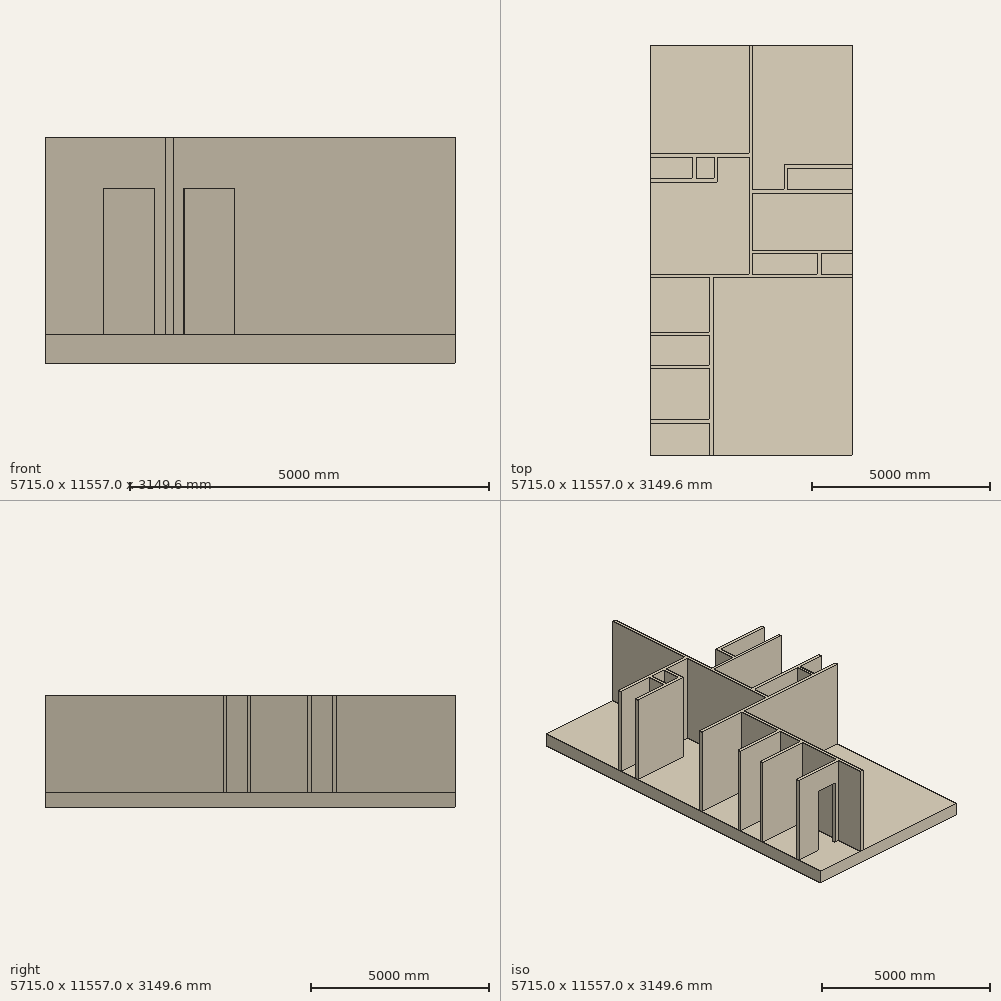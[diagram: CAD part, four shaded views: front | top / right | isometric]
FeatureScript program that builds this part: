
annotation { "Feature Type Name" : "Feature", "Feature Type Description" : "" }
export const myFeature = defineFeature(function(context is Context, id is Id, definition is map)
    precondition{}
    {
        {
            var Q0;
            Q0=qCreatedBy(makeId("Top.planeOp"),FACE);
            var sketch = newSketch(context, id + "F0", { "sketchPlane" : qUnion([Q0])});
            skLineSegment(sketch, "E0.bottom", {"start": v(-2857.5, 5778.5) * mm, "end": v(2857.5, 5778.5) * mm});
            skLineSegment(sketch, "E0.top", {"start": v(-2857.5, -5778.5) * mm, "end": v(2857.5, -5778.5) * mm});
            skLineSegment(sketch, "E0.left", {"start": v(-2857.5, 5778.5) * mm, "end": v(-2857.5, -5778.5) * mm});
            skLineSegment(sketch, "E0.right", {"start": v(2857.5, 5778.5) * mm, "end": v(2857.5, -5778.5) * mm});
            skLineSegment(sketch, "E1", {"start": v(-1079.5, -5778.5) * mm, "end": v(-1079.5, -774.7) * mm});
            skLineSegment(sketch, "E2", {"start": v(-1079.5, -774.7) * mm, "end": v(2857.5, -774.7) * mm});
            skLineSegment(sketch, "E3", {"start": v(-1181.1, -5778.5) * mm, "end": v(-1181.1, -4864.1) * mm});
            skLineSegment(sketch, "E4", {"start": v(-1181.1, -4864.1) * mm, "end": v(-2857.5, -4864.1) * mm});
            skLineSegment(sketch, "E5", {"start": v(-2857.5, -4762.5) * mm, "end": v(-1181.1, -4762.5) * mm});
            skLineSegment(sketch, "E6", {"start": v(-1181.1, -4762.5) * mm, "end": v(-1181.1, -3340.1) * mm});
            skLineSegment(sketch, "E7", {"start": v(-1181.1, -3340.1) * mm, "end": v(-2857.5, -3340.1) * mm});
            skLineSegment(sketch, "E8", {"start": v(-2857.5, -3238.5) * mm, "end": v(-1181.1, -3238.5) * mm});
            skLineSegment(sketch, "E9", {"start": v(-1181.1, -3238.5) * mm, "end": v(-1181.1, -2400.3) * mm});
            skLineSegment(sketch, "E10", {"start": v(-1181.1, -2400.3) * mm, "end": v(-2857.5, -2400.3) * mm});
            skLineSegment(sketch, "E11", {"start": v(-2857.5, -2298.7) * mm, "end": v(-1181.1, -2298.7) * mm});
            skLineSegment(sketch, "E12", {"start": v(-1181.1, -2298.7) * mm, "end": v(-1181.1, -774.7) * mm});
            skLineSegment(sketch, "E13", {"start": v(-1181.1, -774.7) * mm, "end": v(-2857.5, -774.7) * mm});
            skLineSegment(sketch, "E14", {"start": v(2857.5, -673.1) * mm, "end": v(1968.5, -673.1) * mm});
            skLineSegment(sketch, "E15", {"start": v(1968.5, -673.1) * mm, "end": v(1968.5, -88.9) * mm});
            skLineSegment(sketch, "E16", {"start": v(1968.5, -88.9) * mm, "end": v(2857.5, -88.9) * mm});
            skLineSegment(sketch, "E17", {"start": v(2857.5, 12.7) * mm, "end": v(38.1, 12.7) * mm});
            skLineSegment(sketch, "E18", {"start": v(38.1, 12.7) * mm, "end": v(38.1, 1612.9) * mm});
            skLineSegment(sketch, "E19", {"start": v(38.1, 1612.9) * mm, "end": v(2857.5, 1612.9) * mm});
            skLineSegment(sketch, "E20", {"start": v(1866.9, -673.1) * mm, "end": v(1866.9, -88.9) * mm});
            skLineSegment(sketch, "E21", {"start": v(1866.9, -88.9) * mm, "end": v(38.1, -88.9) * mm});
            skLineSegment(sketch, "E22", {"start": v(38.1, -88.9) * mm, "end": v(38.1, -673.1) * mm});
            skLineSegment(sketch, "E23", {"start": v(38.1, -673.1) * mm, "end": v(1866.9, -673.1) * mm});
            skLineSegment(sketch, "E24", {"start": v(-2857.5, -673.1) * mm, "end": v(-63.5, -673.1) * mm});
            skLineSegment(sketch, "E25", {"start": v(-63.5, -673.1) * mm, "end": v(-63.5, 2628.9) * mm});
            skLineSegment(sketch, "E26", {"start": v(-63.5, 2628.9) * mm, "end": v(-952.5, 2628.9) * mm});
            skLineSegment(sketch, "E27", {"start": v(-952.5, 2628.9) * mm, "end": v(-952.5, 1917.7) * mm});
            skLineSegment(sketch, "E28", {"start": v(-952.5, 1917.7) * mm, "end": v(-2857.5, 1917.7) * mm});
            skLineSegment(sketch, "E29.bottom", {"start": v(-1054.1, 2019.3) * mm, "end": v(-1562.1, 2019.3) * mm});
            skLineSegment(sketch, "E29.top", {"start": v(-1054.1, 2628.9) * mm, "end": v(-1562.1, 2628.9) * mm});
            skLineSegment(sketch, "E29.left", {"start": v(-1054.1, 2019.3) * mm, "end": v(-1054.1, 2628.9) * mm});
            skLineSegment(sketch, "E29.right", {"start": v(-1562.1, 2019.3) * mm, "end": v(-1562.1, 2628.9) * mm});
            skLineSegment(sketch, "E30", {"start": v(-2857.5, 2019.3) * mm, "end": v(-1663.7, 2019.3) * mm});
            skLineSegment(sketch, "E31", {"start": v(-1663.7, 2019.3) * mm, "end": v(-1663.7, 2628.9) * mm});
            skLineSegment(sketch, "E32", {"start": v(-1663.7, 2628.9) * mm, "end": v(-2857.5, 2628.9) * mm});
            skLineSegment(sketch, "E33", {"start": v(-2857.5, 2730.5) * mm, "end": v(-63.5, 2730.5) * mm});
            skLineSegment(sketch, "E34", {"start": v(-63.5, 2730.5) * mm, "end": v(-63.5, 5778.5) * mm});
            skLineSegment(sketch, "E35", {"start": v(38.1, 1714.5) * mm, "end": v(38.1, 5778.5) * mm});
            skLineSegment(sketch, "E36", {"start": v(38.1, 1714.5) * mm, "end": v(927.1, 1714.5) * mm});
            skLineSegment(sketch, "E37", {"start": v(927.1, 1714.5) * mm, "end": v(927.1, 2425.7) * mm});
            skLineSegment(sketch, "E38", {"start": v(927.1, 2425.7) * mm, "end": v(2857.5, 2425.7) * mm});
            skLineSegment(sketch, "E39", {"start": v(2857.5, 1714.5) * mm, "end": v(1028.7, 1714.5) * mm});
            skLineSegment(sketch, "E40", {"start": v(1028.7, 1714.5) * mm, "end": v(1028.7, 2324.1) * mm});
            skLineSegment(sketch, "E41", {"start": v(1028.7, 2324.1) * mm, "end": v(2857.5, 2324.1) * mm});
            skSolve(sketch);
        }
        {
            var Q0;
            Q0 = qSketchRegion(id + "F0", true);
            var Q1;
            Q1=makeQuery(id+"F0.imprint","IMPRINT",FACE,{"disambiguationData":[TD([[makeQuery(id+"F0.imprint","IMPRINT",EDGE,{"derivedFrom":sQuery(id+"F0.wireOp",EDGE,"E29.bottom")}),-1.0]])]});
            var Q2;
            Q2=makeQuery(id+"F0.imprint","IMPRINT",FACE,{"disambiguationData":[TD([[makeQuery(id+"F0.imprint","IMPRINT",EDGE,{"derivedFrom":sQuery(id+"F0.wireOp",EDGE,"E20")}),1.0]])]});
            extrude(context, id + "F1", {"entities" : qUnion([Q0, Q1, Q2]), "oppositeDirection" : true, "depth" : 406.4 * mm});
        }
        {
            var Q0;
            {var subQ19=sQuery(id+"F0.wireOp",EDGE,"E1");Q0=makeQuery(id+"F0.imprint","IMPRINT",FACE,{"disambiguationData":[TD([[makeQuery(id+"F0.imprint","IMPRINT",EDGE,{"derivedFrom":subQ19}),1.0]])]});}
            extrude(context, id + "F2", {"entities" : qUnion([Q0]), "depth" : 2743.2 * mm});
        }
        {
            var Q0;
            Q0=makeQuery(id+"F2.opExtrude","SWEPT_FACE",FACE,{"disambiguationData":[OSD([sQuery(id+"F0.wireOp",EDGE,"E2")])]});
            var sketch = newSketch(context, id + "F3", { "sketchPlane" : qUnion([Q0])});
            skLineSegment(sketch, "E42", {"start": v(-927.1, 0) * mm, "end": v(-927.1, 2032) * mm});
            skLineSegment(sketch, "E43", {"start": v(-927.1, 2032) * mm, "end": v(-215.9, 2032) * mm});
            skLineSegment(sketch, "E44", {"start": v(-215.9, 2032) * mm, "end": v(-215.9, 0) * mm});
            skSolve(sketch);
        }
        {
            var Q0;
            {var subQ0=sQuery(id+"F3.wireOp",EDGE,"E42");Q0=makeQuery(id+"F3.imprint","IMPRINT",FACE,{"disambiguationData":[TD([[makeQuery(id+"F3.imprint","IMPRINT",EDGE,{"derivedFrom":subQ0}),-1.0]])]});}
            extrude(context, id + "F4", {"entities" : qUnion([Q0]), "operationType" : NewBodyOperationType.REMOVE, "endBound" : BoundingType.UP_TO_NEXT, "oppositeDirection" : true, "depth" : 25.4 * mm});
        }
        {
            var Q0;
            Q0=makeQuery(id+"F2.opExtrude","SWEPT_FACE",FACE,{"disambiguationData":[OSD([sQuery(id+"F0.wireOp",EDGE,"E4")])]});
            var sketch = newSketch(context, id + "F5", { "sketchPlane" : qUnion([Q0])});
            skLineSegment(sketch, "E45", {"start": v(-2044.7, 0) * mm, "end": v(-2044.7, 2032) * mm});
            skLineSegment(sketch, "E46", {"start": v(-2044.7, 2032) * mm, "end": v(-1333.5, 2032) * mm});
            skLineSegment(sketch, "E47", {"start": v(-1333.5, 2032) * mm, "end": v(-1333.5, 0) * mm});
            skSolve(sketch);
        }
        {
            var Q0;
            {var subQ0=sQuery(id+"F5.wireOp",EDGE,"E45");Q0=makeQuery(id+"F5.imprint","IMPRINT",FACE,{"disambiguationData":[TD([[makeQuery(id+"F5.imprint","IMPRINT",EDGE,{"derivedFrom":subQ0}),-1.0]])]});}
            extrude(context, id + "F6", {"entities" : qUnion([Q0]), "operationType" : NewBodyOperationType.REMOVE, "endBound" : BoundingType.UP_TO_NEXT, "oppositeDirection" : true, "depth" : 25.4 * mm});
        }
    });
